# Revit family: Water_Heater-Rinnai-Luxury_Line-Residential-Tankless-V94i
name_source: partatom
category: Mechanical Equipment
revit_build: Autodesk Revit MEP 2012 (Build: 20110916_2132(x64)
units: mm (PartAtom-declared; Revit-internal decimal feet)

## types (1)
- Standard
    04 CSI = 22 34 13
    95 CSI = 15480
    Air Supply Connector = Air Supply Connection
    Air Supply Diameter = 2 55/64"
    Applicable Altitude Range = 0-10,200ft (0-3,109m)
    Assembly Code = D3010500
    Clearance for Back = 0"
    Clearance for Exhaust = 0"
    Clearance for Front = 6"
    Clearance for Ground or Bottom = 12"
    Clearance for Sides = 1/2"
    Clearance for Top = 6"
    Cold Water Connector = Cold Water Connection Inlet
    Cold Water Inlet Diameter = 3/4"
    Cold Water Inlet Radius = 3/8"
    Combustibles = Yes
    Combustion Air = Indoor
    Default Elevation = 48"
    Depth = 9"
    Description = Tankless Water Heater
    Door = Metal - Rinnai - Aluminum - Polished Sliver
    Dry Weight = 46.30 lb
    Electrical Consumption Range = Normal: 97 w, Standby: 2 w
    Energy Factor = 0.82
    Exhaust Vent Length Max or Equivalent = 492"
    Exhaust Vent Length Note = Concentric venting, 1one 90° Elbow equal to 6', one 45° elbow equal to 3'
    Flow Rate = 9.80 GPM
    Frequency = 60 Hz
    Gas Connection = Gas Connection
    Gas Input Range = 10,300 - 199,000 BTU/h
    Gas Input Rate = 199000.0 Btu/h
    Gas Manifold Pressure High Fire = 2.9" (NG); 4.7" (Propane)
    Gas Manifold Pressure Low Fire = .61" (NG); .87" (Propane)
    Gas Supply Pressure Max = 10.5" (NG); 13.5" (Propane)
    Gas Supply Pressure Min = 4" (NG); 8" (Propane)
    Gas Supply Radius = 3/8"
    Hardware = Metal - Rinnai - Aluminum Frame - Painted White
    Height = 23"
    Hot Water Connector = Hot Water Connection Outlet
    Hot Water Flow Rate Range = Min - .26 GPM, Min Activation - .4 GPM, Max - 9.8 GPM
    Hot Water Outlet Diameter = 3/4"
    Hot Water Outlet Radius = 3/8"
    Ignition System = Direct electronic ignition
    Installation Location = Indoor only
    Installation URL = https://www.rinnai.us
    Interference = <By Category>
    Liquid Propane = No
    Manufacturer = Rinnai America Corporation
    Manufacturer Fax = 678-829-1666
    Max Amperage = 4 A
    Max Amperage Note = 4 A w/o pump, 8A with pump
    Model = REU-VC2837FFU-US
    Natural Gas = Yes
    Panel = Metal - Rinnai - Aluminum Frame - Painted White
    Product Page URL = https://rinnai.us
    Spec Sheet URL = https://www.rinnai.us
    Subcategory = Tankless Water Heaters
    Supply Air Radius = 1 55/128"
    Temperature Settings = 98° - 120° F
    URL = http://www.rinnai.us
    Unit = Metal - Rinnai - Aluminum Frame - Painted White
    Vent Connection Diameter = 4 251/256"
    Vent Connection Radius = 2 125/256"
    Vent Connector = Vent Connection
    Venting = Concentric
    Voltage = 120 V
    Warranty URL = https://www.rinnai.us
    Water Supply Pressure = 0.00 psi
    Wattage = 97 W
    Width = 14"
    ecoScorecard Product Page = http://products.ecoscorecard.com
    ecoScorecard_data = http://products.ecoscorecard.com

## geometry (parser evidence)
native form markers: Blend x2, Sweep x17
no freeform markers — native parametric forms only
